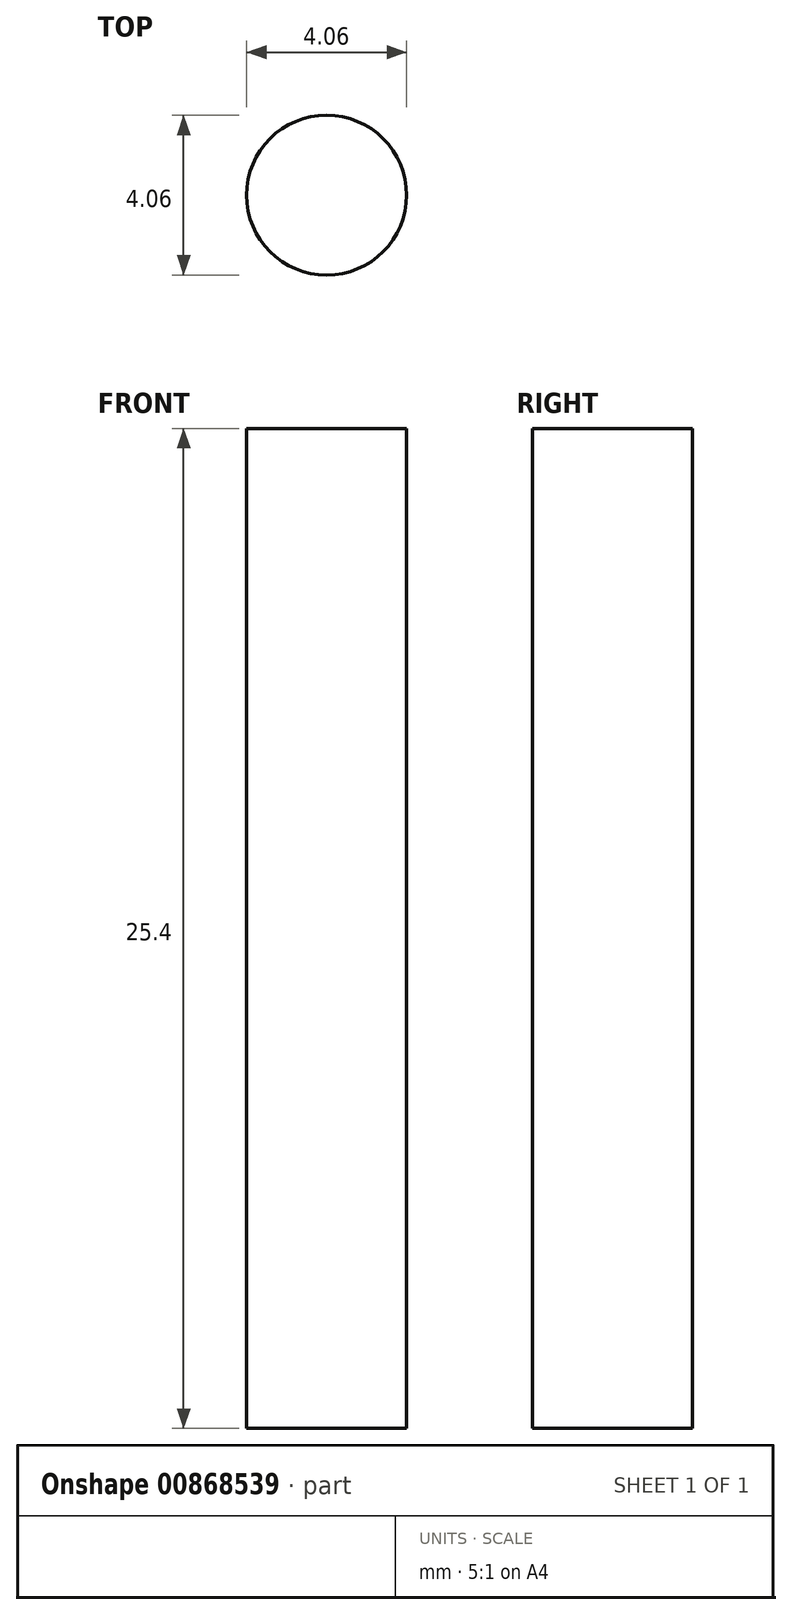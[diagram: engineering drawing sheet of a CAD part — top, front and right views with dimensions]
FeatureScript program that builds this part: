
annotation { "Feature Type Name" : "Feature", "Feature Type Description" : "" }
export const myFeature = defineFeature(function(context is Context, id is Id, definition is map)
    precondition{}
    {
        {
            var Q0;
            Q0=qCreatedBy(makeId("Top.planeOp"),FACE);
            var sketch = newSketch(context, id + "F0", { "sketchPlane" : qUnion([Q0])});
            skCircle(sketch, "E0", {"center": v(0, 0) * mm, "radius": 2.03 * mm});
            skSolve(sketch);
        }
        {
            var Q0;
            Q0=makeQuery(id+"F0.imprint","IMPRINT",FACE,{"disambiguationData":[TD([[makeQuery(id+"F0.imprint","IMPRINT",EDGE,{"derivedFrom":sQuery(id+"F0.wireOp",EDGE,"E0")}),1.0]])]});
            extrude(context, id + "F1", {"entities" : qUnion([Q0]), "depth" : 25.4 * mm, "offsetDistance" : 25.4 * mm});
        }
    });
